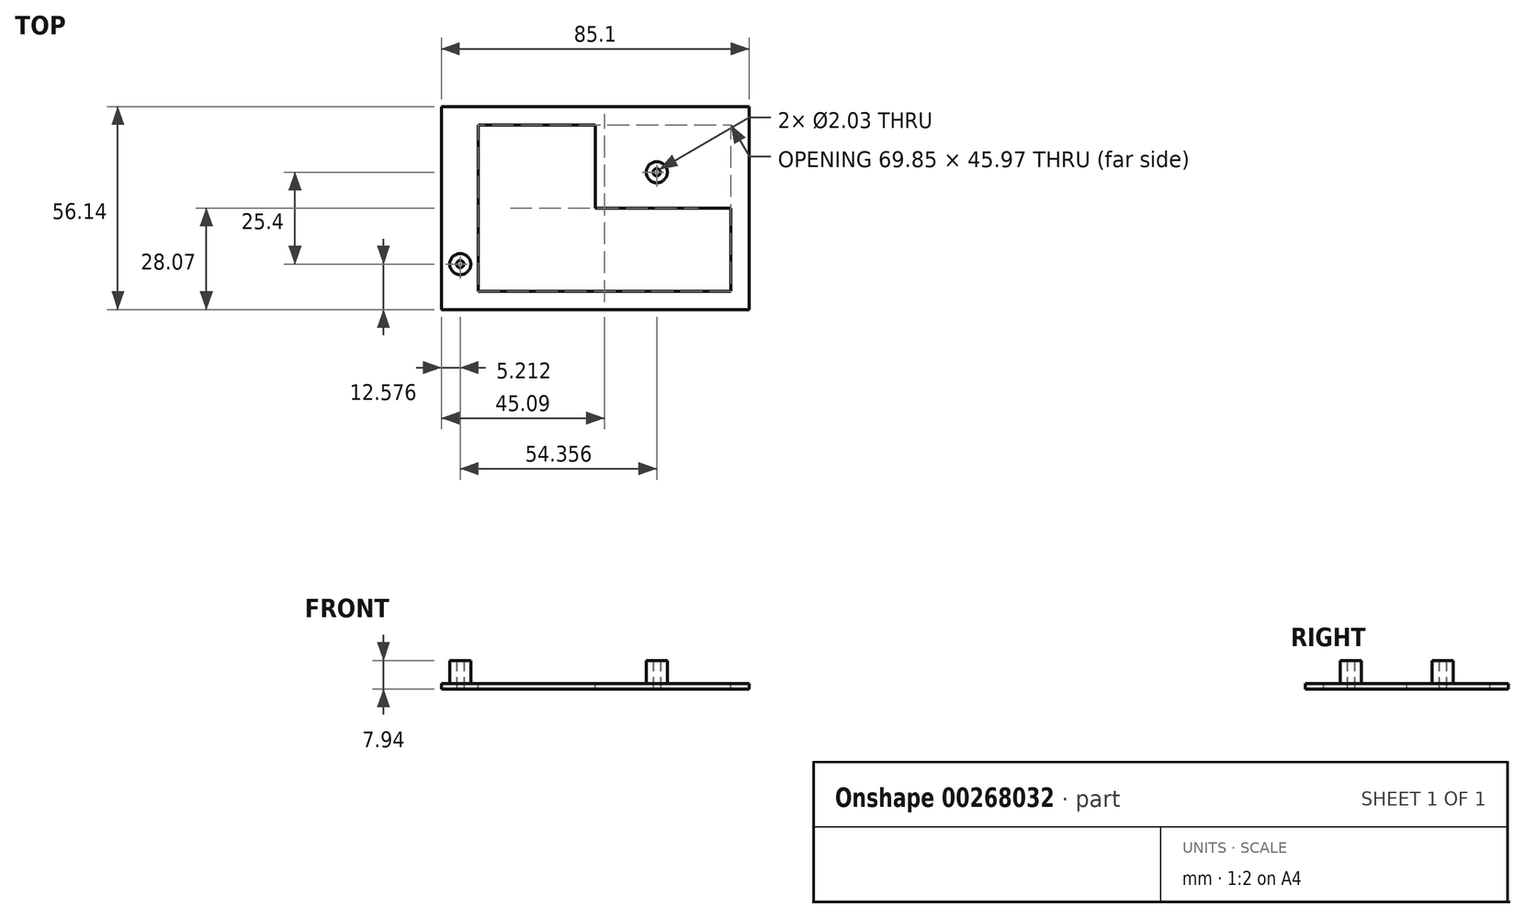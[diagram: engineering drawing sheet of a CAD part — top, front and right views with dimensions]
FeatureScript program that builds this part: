
annotation { "Feature Type Name" : "Feature", "Feature Type Description" : "" }
export const myFeature = defineFeature(function(context is Context, id is Id, definition is map)
    precondition{}
    {
        {
            var Q0;
            Q0=qCreatedBy(makeId("Top.planeOp"),FACE);
            var sketch = newSketch(context, id + "F0", { "sketchPlane" : qUnion([Q0])});
            skLineSegment(sketch, "E0.bottom", {"start": v(42.55, 28.07) * mm, "end": v(-42.55, 28.07) * mm});
            skLineSegment(sketch, "E0.top", {"start": v(42.55, -28.07) * mm, "end": v(-42.55, -28.07) * mm});
            skLineSegment(sketch, "E0.left", {"start": v(42.55, 28.07) * mm, "end": v(42.55, -28.07) * mm});
            skLineSegment(sketch, "E0.right", {"start": v(-42.55, 28.07) * mm, "end": v(-42.55, -28.07) * mm});
            skPoint(sketch, "E0.middle", {"position": v(0, 0) * mm});
            skSolve(sketch);
        }
        {
            var Q0;
            Q0=makeQuery(id+"F0.imprint","IMPRINT",FACE,{"disambiguationData":[TD([[makeQuery(id+"F0.imprint","IMPRINT",EDGE,{"derivedFrom":sQuery(id+"F0.wireOp",EDGE,"E0.bottom")}),1.0]])]});
            extrude(context, id + "F1", {"entities" : qUnion([Q0]), "depth" : 1.59 * mm});
        }
        {
            var Q0;
            Q0=makeQuery(id+"F1.opExtrude","CAP_FACE",FACE,{"disambiguationData":[OSD([sQuery(id+"F0.wireOp",EDGE,"E0.bottom"),sQuery(id+"F0.wireOp",EDGE,"E0.top"),sQuery(id+"F0.wireOp",EDGE,"E0.left"),sQuery(id+"F0.wireOp",EDGE,"E0.right")])],"isStart":false});
            var sketch = newSketch(context, id + "F2", { "sketchPlane" : qUnion([Q0])});
            skLineSegment(sketch, "E1.top", {"start": v(-37.34, -28.07) * mm, "end": v(42.55, -28.07) * mm, "construction": true});
            skLineSegment(sketch, "E1.left", {"start": v(-37.34, -15.5) * mm, "end": v(-37.34, -28.07) * mm, "construction": true});
            skLineSegment(sketch, "E1.right", {"start": v(42.55, -15.5) * mm, "end": v(42.55, -28.07) * mm, "construction": true});
            skCircle(sketch, "E2", {"center": v(-37.34, -15.5) * mm, "radius": 1.02 * mm});
            skCircle(sketch, "E3", {"center": v(-37.34, -15.5) * mm, "radius": 2.92 * mm});
            skCircle(sketch, "E4", {"center": v(17.02, 9.9) * mm, "radius": 1.02 * mm});
            skCircle(sketch, "E5", {"center": v(17.02, 9.9) * mm, "radius": 2.92 * mm});
            skLineSegment(sketch, "E6.bottom", {"start": v(42.55, -28.07) * mm, "end": v(-42.55, -28.07) * mm, "construction": true});
            skLineSegment(sketch, "E6.top", {"start": v(42.55, 28.07) * mm, "end": v(-42.55, 28.07) * mm, "construction": true});
            skLineSegment(sketch, "E6.left", {"start": v(42.55, -28.07) * mm, "end": v(42.55, 28.07) * mm, "construction": true});
            skLineSegment(sketch, "E6.right", {"start": v(-42.54, -28.07) * mm, "end": v(-42.54, 28.07) * mm, "construction": true});
            skLineSegment(sketch, "E7", {"start": v(-42.55, -15.5) * mm, "end": v(-37.34, -15.5) * mm, "construction": true});
            skLineSegment(sketch, "E8", {"start": v(-42.55, 9.9) * mm, "end": v(17.02, 9.9) * mm, "construction": true});
            skLineSegment(sketch, "E9", {"start": v(17.02, -28.07) * mm, "end": v(17.02, 9.9) * mm, "construction": true});
            skSolve(sketch);
        }
        {
            var Q0;
            Q0=makeQuery(id+"F2.imprint","IMPRINT",FACE,{"disambiguationData":[TD([[makeQuery(id+"F2.imprint","IMPRINT",EDGE,{"derivedFrom":sQuery(id+"F2.wireOp",EDGE,"E4")}),-1.0]])]});
            var Q1;
            Q1=makeQuery(id+"F2.imprint","IMPRINT",FACE,{"disambiguationData":[TD([[makeQuery(id+"F2.imprint","IMPRINT",EDGE,{"derivedFrom":sQuery(id+"F2.wireOp",EDGE,"E2")}),-1.0]])]});
            var Q2;
            Q2=makeQuery(id+"F2.imprint","IMPRINT",FACE,{"disambiguationData":[TD([[makeQuery(id+"F2.imprint","IMPRINT",EDGE,{"derivedFrom":sQuery(id+"F2.wireOp",EDGE,"f221bf73-ab4d-45dd-a228-82dda82d936a")}),-1.0]])]});
            var Q3;
            Q3=makeQuery(id+"F2.imprint","IMPRINT",FACE,{"disambiguationData":[TD([[makeQuery(id+"F2.imprint","IMPRINT",EDGE,{"derivedFrom":sQuery(id+"F2.wireOp",EDGE,"a98f36b7-2298-438e-b609-409c075824e1")}),-1.0]])]});
            extrude(context, id + "F3", {"entities" : qUnion([Q0, Q1, Q2, Q3]), "operationType" : NewBodyOperationType.ADD, "depth" : 6.35 * mm});
        }
        {
            var Q0;
            Q0=makeQuery(id+"F2.imprint","IMPRINT",FACE,{"disambiguationData":[TD([[makeQuery(id+"F2.imprint","IMPRINT",EDGE,{"derivedFrom":sQuery(id+"F2.wireOp",EDGE,"E2")}),1.0]])]});
            var Q1;
            Q1=makeQuery(id+"F2.imprint","IMPRINT",FACE,{"disambiguationData":[TD([[makeQuery(id+"F2.imprint","IMPRINT",EDGE,{"derivedFrom":sQuery(id+"F2.wireOp",EDGE,"f221bf73-ab4d-45dd-a228-82dda82d936a")}),1.0]])]});
            var Q2;
            Q2=makeQuery(id+"F2.imprint","IMPRINT",FACE,{"disambiguationData":[TD([[makeQuery(id+"F2.imprint","IMPRINT",EDGE,{"derivedFrom":sQuery(id+"F2.wireOp",EDGE,"E4")}),1.0]])]});
            var Q3;
            Q3=makeQuery(id+"F2.imprint","IMPRINT",FACE,{"disambiguationData":[TD([[makeQuery(id+"F2.imprint","IMPRINT",EDGE,{"derivedFrom":sQuery(id+"F2.wireOp",EDGE,"a98f36b7-2298-438e-b609-409c075824e1")}),1.0]])]});
            extrude(context, id + "F4", {"entities" : qUnion([Q0, Q1, Q2, Q3]), "operationType" : NewBodyOperationType.REMOVE, "oppositeDirection" : true, "depth" : 6.35 * mm});
        }
        {
            var Q0;
            Q0=makeQuery(id+"F1.opExtrude","CAP_FACE",FACE,{"disambiguationData":[OSD([sQuery(id+"F0.wireOp",EDGE,"E0.bottom"),sQuery(id+"F0.wireOp",EDGE,"E0.top"),sQuery(id+"F0.wireOp",EDGE,"E0.left"),sQuery(id+"F0.wireOp",EDGE,"E0.right")])],"isStart":false});
            var sketch = newSketch(context, id + "F5", { "sketchPlane" : qUnion([Q0])});
            skLineSegment(sketch, "E10.bottom", {"start": v(0, 0) * mm, "end": v(-32.39, 0) * mm});
            skLineSegment(sketch, "E10.top", {"start": v(0, -22.99) * mm, "end": v(-32.38, -22.99) * mm});
            skLineSegment(sketch, "E10.left", {"start": v(0, 0) * mm, "end": v(0, -22.99) * mm});
            skLineSegment(sketch, "E10.right", {"start": v(-32.39, 0) * mm, "end": v(-32.39, -22.99) * mm});
            skLineSegment(sketch, "E11.top", {"start": v(0, 22.99) * mm, "end": v(-32.39, 22.99) * mm});
            skLineSegment(sketch, "E11.left", {"start": v(0, 0) * mm, "end": v(0, 22.99) * mm});
            skLineSegment(sketch, "E11.right", {"start": v(-32.39, 0) * mm, "end": v(-32.39, 22.99) * mm});
            skLineSegment(sketch, "E12.bottom", {"start": v(0, 0) * mm, "end": v(37.47, 0) * mm});
            skLineSegment(sketch, "E12.top", {"start": v(0, -22.99) * mm, "end": v(37.47, -22.99) * mm});
            skLineSegment(sketch, "E12.right", {"start": v(37.47, 0) * mm, "end": v(37.47, -22.99) * mm});
            skLineSegment(sketch, "E13.bottom", {"start": v(-32.39, 22.99) * mm, "end": v(-42.55, 22.99) * mm, "construction": true});
            skLineSegment(sketch, "E13.top", {"start": v(-32.39, 28.07) * mm, "end": v(-42.55, 28.07) * mm, "construction": true});
            skLineSegment(sketch, "E13.left", {"start": v(-32.39, 22.99) * mm, "end": v(-32.39, 28.07) * mm, "construction": true});
            skLineSegment(sketch, "E13.right", {"start": v(-42.55, 22.99) * mm, "end": v(-42.55, 28.07) * mm, "construction": true});
            skLineSegment(sketch, "E14.bottom", {"start": v(37.47, -22.99) * mm, "end": v(42.55, -22.99) * mm, "construction": true});
            skLineSegment(sketch, "E14.top", {"start": v(37.47, -28.07) * mm, "end": v(42.55, -28.07) * mm, "construction": true});
            skLineSegment(sketch, "E14.left", {"start": v(37.47, -22.99) * mm, "end": v(37.47, -28.07) * mm, "construction": true});
            skLineSegment(sketch, "E14.right", {"start": v(42.55, -22.99) * mm, "end": v(42.55, -28.07) * mm, "construction": true});
            skLineSegment(sketch, "E15.bottom", {"start": v(-32.38, -22.99) * mm, "end": v(-42.55, -22.99) * mm, "construction": true});
            skLineSegment(sketch, "E15.top", {"start": v(-32.39, -28.07) * mm, "end": v(-42.55, -28.07) * mm, "construction": true});
            skLineSegment(sketch, "E15.left", {"start": v(-32.39, -22.99) * mm, "end": v(-32.39, -28.07) * mm, "construction": true});
            skLineSegment(sketch, "E15.right", {"start": v(-42.55, -22.99) * mm, "end": v(-42.55, -28.07) * mm, "construction": true});
            skLineSegment(sketch, "E16.bottom", {"start": v(0, 0) * mm, "end": v(10.16, 0) * mm});
            skLineSegment(sketch, "E16.top", {"start": v(0, 22.99) * mm, "end": v(10.16, 22.99) * mm});
            skLineSegment(sketch, "E16.right", {"start": v(10.16, 0) * mm, "end": v(10.16, 22.99) * mm});
            skLineSegment(sketch, "E17.bottom", {"start": v(10.16, 0) * mm, "end": v(37.47, 0) * mm});
            skLineSegment(sketch, "E17.top", {"start": v(10.16, 5.08) * mm, "end": v(37.47, 5.08) * mm});
            skLineSegment(sketch, "E17.left", {"start": v(10.16, 0) * mm, "end": v(10.16, 5.08) * mm});
            skLineSegment(sketch, "E17.right", {"start": v(37.47, 0) * mm, "end": v(37.47, 5.08) * mm});
            skSolve(sketch);
        }
        {
            var Q0;
            Q0=makeQuery(id+"F5.imprint","IMPRINT",FACE,{"disambiguationData":[TD([[makeQuery(id+"F5.imprint","IMPRINT",EDGE,{"derivedFrom":sQuery(id+"F5.wireOp",EDGE,"E10.bottom")}),-1.0]])]});
            var Q1;
            Q1=makeQuery(id+"F5.imprint","IMPRINT",FACE,{"disambiguationData":[TD([[makeQuery(id+"F5.imprint","IMPRINT",EDGE,{"derivedFrom":sQuery(id+"F5.wireOp",EDGE,"E16.bottom")}),1.0]])]});
            var Q2;
            Q2=makeQuery(id+"F5.imprint","IMPRINT",FACE,{"disambiguationData":[TD([[makeQuery(id+"F5.imprint","IMPRINT",EDGE,{"derivedFrom":sQuery(id+"F5.wireOp",EDGE,"E17.bottom")}),1.0]])]});
            var Q3;
            Q3=makeQuery(id+"F5.imprint","IMPRINT",FACE,{"disambiguationData":[TD([[makeQuery(id+"F5.imprint","IMPRINT",EDGE,{"derivedFrom":sQuery(id+"F5.wireOp",EDGE,"E12.top")}),1.0]])]});
            var Q4;
            Q4=makeQuery(id+"F5.imprint","IMPRINT",FACE,{"disambiguationData":[TD([[makeQuery(id+"F5.imprint","IMPRINT",EDGE,{"derivedFrom":sQuery(id+"F5.wireOp",EDGE,"E10.top")}),-1.0]])]});
            extrude(context, id + "F6", {"entities" : qUnion([Q0, Q1, Q2, Q3, Q4]), "operationType" : NewBodyOperationType.REMOVE, "oppositeDirection" : true, "depth" : 6.35 * mm});
        }
    });
